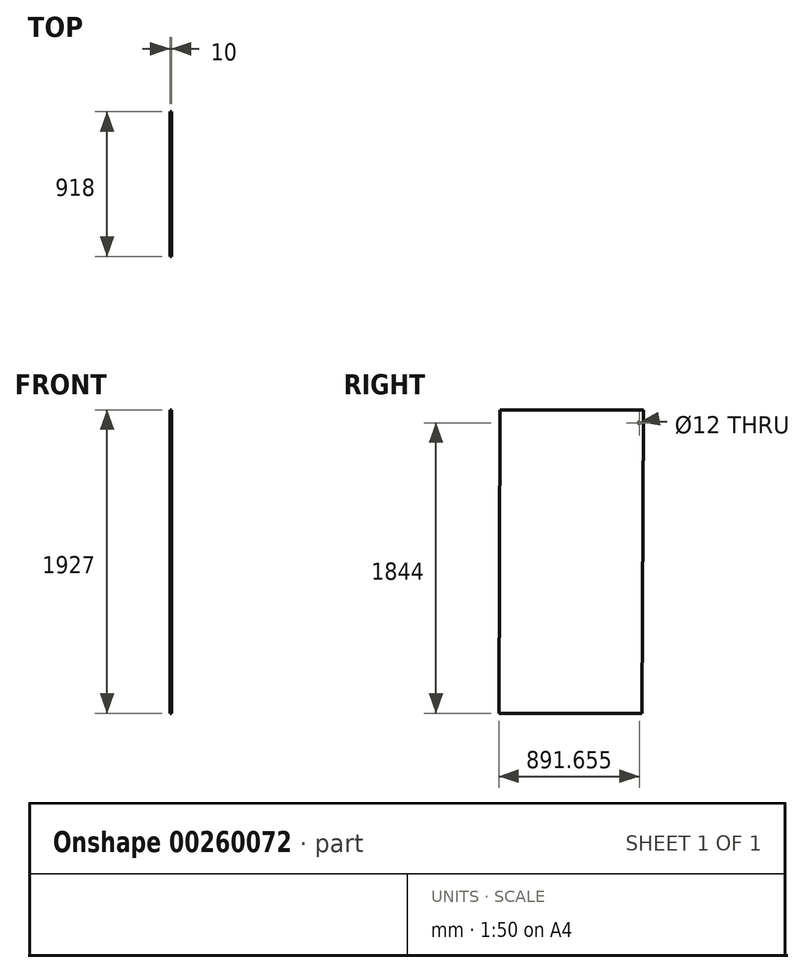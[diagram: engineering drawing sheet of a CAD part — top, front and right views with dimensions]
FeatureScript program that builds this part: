
annotation { "Feature Type Name" : "Feature", "Feature Type Description" : "" }
export const myFeature = defineFeature(function(context is Context, id is Id, definition is map)
    precondition{}
    {
        {
            var Q0;
            Q0=qCreatedBy(makeId("Right.planeOp"),FACE);
            var sketch = newSketch(context, id + "F0", { "sketchPlane" : qUnion([Q0]), "disableImprinting" : false});
            skLineSegment(sketch, "E0.bottom", {"start": v(495, -527.5) * mm, "end": v(-415, -527.5) * mm});
            skLineSegment(sketch, "E0.top", {"start": v(503, 1399.5) * mm, "end": v(-407, 1399.5) * mm});
            skLineSegment(sketch, "E1", {"start": v(-415, -527.5) * mm, "end": v(-407, 1399.5) * mm});
            skLineSegment(sketch, "E2", {"start": v(503, 1399.5) * mm, "end": v(495, -527.5) * mm});
            skSolve(sketch);
        }
        {
            var Q0;
            Q0 = qSketchRegion(id + "F0", true);
            extrude(context, id + "F1", {"entities" : qUnion([Q0]), "depth" : 10 * mm, "offsetDistance" : 25 * mm});
        }
        {
            var Q0;
            Q0=makeQuery(id+"F1.opExtrude","CAP_FACE",FACE,{"disambiguationData":[OSD([sQuery(id+"F0.wireOp",EDGE,"E0.bottom"),sQuery(id+"F0.wireOp",EDGE,"E0.top"),sQuery(id+"F0.wireOp",EDGE,"E0.left"),sQuery(id+"F0.wireOp",EDGE,"E1")])],"isStart":false});
            var sketch = newSketch(context, id + "F2", { "sketchPlane" : qUnion([Q0]), "disableImprinting" : false});
            skCircle(sketch, "E3", {"center": v(476.66, 1316.5) * mm, "radius": 6 * mm});
            skSolve(sketch);
        }
        {
            var Q0;
            Q0 = qSketchRegion(id + "F2", true);
            extrude(context, id + "F3", {"entities" : qUnion([Q0]), "operationType" : NewBodyOperationType.REMOVE, "endBound" : BoundingType.UP_TO_NEXT, "oppositeDirection" : true, "depth" : 25 * mm, "offsetDistance" : 25 * mm});
        }
    });
